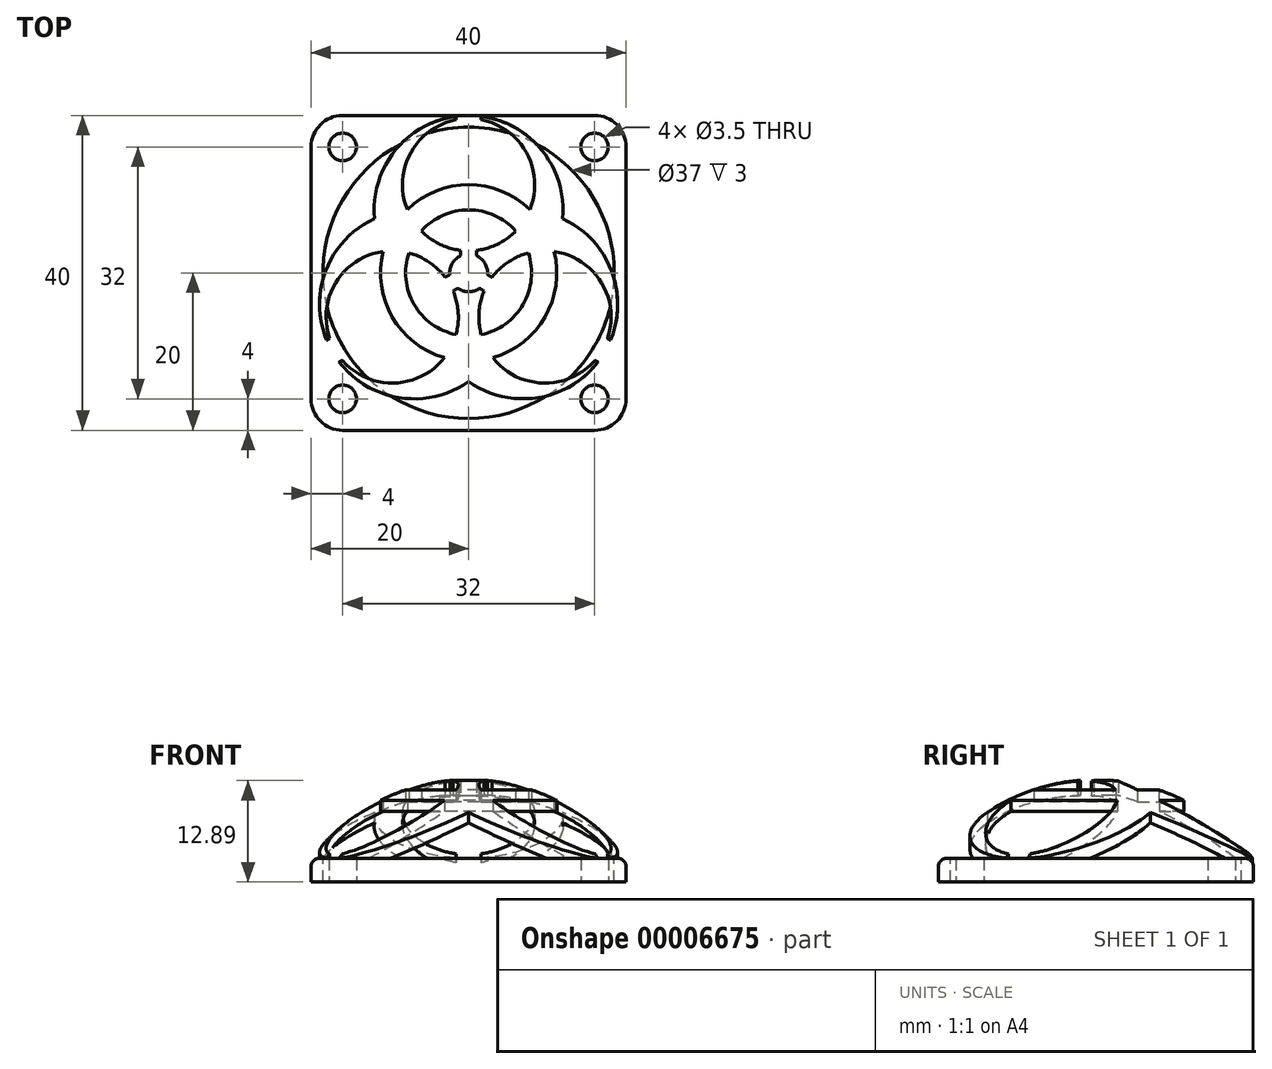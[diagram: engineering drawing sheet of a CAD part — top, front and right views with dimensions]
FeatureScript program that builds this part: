
annotation { "Feature Type Name" : "Feature", "Feature Type Description" : "" }
export const myFeature = defineFeature(function(context is Context, id is Id, definition is map)
    precondition{}
    {
        {
            var Q0;
            Q0=qCreatedBy(makeId("Top.planeOp"),FACE);
            var sketch = newSketch(context, id + "F0", { "sketchPlane" : qUnion([Q0])});
            skLineSegment(sketch, "E0.bottom", {"start": v(0, 0) * mm, "end": v(40, 0) * mm});
            skLineSegment(sketch, "E0.top", {"start": v(0, 40) * mm, "end": v(40, 40) * mm});
            skLineSegment(sketch, "E0.left", {"start": v(0, 0) * mm, "end": v(0, 40) * mm});
            skLineSegment(sketch, "E0.right", {"start": v(40, 0) * mm, "end": v(40, 40) * mm});
            skSolve(sketch);
        }
        {
            var Q0;
            Q0 = qSketchRegion(id + "F0", true);
            extrude(context, id + "F1", {"entities" : qUnion([Q0]), "depth" : 3 * mm});
        }
        {
            var Q0;
            Q0=makeQuery(id+"F1.opExtrude","CAP_FACE",FACE,{"disambiguationData":[OSD([sQuery(id+"F0.wireOp",EDGE,"E0.bottom"),sQuery(id+"F0.wireOp",EDGE,"E0.top"),sQuery(id+"F0.wireOp",EDGE,"E0.left"),sQuery(id+"F0.wireOp",EDGE,"E0.right")])],"isStart":false});
            var sketch = newSketch(context, id + "F2", { "sketchPlane" : qUnion([Q0])});
            skCircle(sketch, "E1", {"center": v(20, 20) * mm, "radius": 18.5 * mm});
            skSolve(sketch);
        }
        {
            var Q0;
            Q0 = qSketchRegion(id + "F2", true);
            extrude(context, id + "F3", {"entities" : qUnion([Q0]), "operationType" : NewBodyOperationType.REMOVE, "endBound" : BoundingType.THROUGH_ALL, "oppositeDirection" : true, "depth" : 25 * mm});
        }
        {
            var Q0;
            Q0=makeQuery(id+"F1.opExtrude","SWEPT_EDGE",EDGE,{"disambiguationData":[OSD([sQuery(id+"F0.wireOp",EDGE,"E0.top"),sQuery(id+"F0.wireOp",EDGE,"E0.right")])]});
            var Q1;
            Q1=makeQuery(id+"F1.opExtrude","SWEPT_EDGE",EDGE,{"disambiguationData":[OSD([sQuery(id+"F0.wireOp",EDGE,"E0.bottom"),sQuery(id+"F0.wireOp",EDGE,"E0.right")])]});
            var Q2;
            Q2=makeQuery(id+"F1.opExtrude","SWEPT_EDGE",EDGE,{"disambiguationData":[OSD([sQuery(id+"F0.wireOp",EDGE,"E0.top"),sQuery(id+"F0.wireOp",EDGE,"E0.left")])]});
            var Q3;
            Q3=makeQuery(id+"F1.opExtrude","SWEPT_EDGE",EDGE,{"disambiguationData":[OSD([sQuery(id+"F0.wireOp",EDGE,"E0.bottom"),sQuery(id+"F0.wireOp",EDGE,"E0.left")])]});
            fillet(context, id + "F4", {"entities" : qUnion([Q0, Q1, Q2, Q3]), "radius" : 4 * mm, "tangentPropagation" : true, "allowEdgeOverflow" : false});
        }
        {
            var Q0;
            Q0=makeQuery(id+"F1.opExtrude","CAP_FACE",FACE,{"disambiguationData":[OSD([sQuery(id+"F0.wireOp",EDGE,"E0.bottom"),sQuery(id+"F0.wireOp",EDGE,"E0.top"),sQuery(id+"F0.wireOp",EDGE,"E0.left"),sQuery(id+"F0.wireOp",EDGE,"E0.right")])],"isStart":true});
            var sketch = newSketch(context, id + "F5", { "sketchPlane" : qUnion([Q0])});
            skArc(sketch, "E2", {"start": v(21, -22.18) * mm, "mid": v(22.08, -21.2) * mm, "end": v(22.39, -19.78) * mm});
            skArc(sketch, "E3", {"start": v(18.4, -12.16) * mm, "mid": v(13.07, -16) * mm, "end": v(12.41, -22.53) * mm});
            skArc(sketch, "E4", {"start": v(30.87, -22.72) * mm, "mid": v(29.7, -14.4) * mm, "end": v(23.08, -9.23) * mm});
            skArc(sketch, "E5", {"start": v(31.95, -26.9) * mm, "mid": v(38.1, -20.4) * mm, "end": v(38.03, -11.44) * mm});
            skArc(sketch, "E6", {"start": v(20, -6.2) * mm, "mid": v(11.3, -4.13) * mm, "end": v(3.57, -8.67) * mm});
            skArc(sketch, "E7", {"start": v(12.21, -28.05) * mm, "mid": v(12.62, -35.2) * mm, "end": v(18.4, -39.45) * mm});
            skArc(sketch, "E8", {"start": v(21.6, -12.16) * mm, "mid": v(21.32, -14.96) * mm, "end": v(21.98, -17.7) * mm});
            skArc(sketch, "E9", {"start": v(12.41, -22.53) * mm, "mid": v(14.98, -21.38) * mm, "end": v(17.02, -19.44) * mm});
            skArc(sketch, "E10.trimOffspring", {"start": v(16.92, -9.23) * mm, "mid": v(10.3, -14.4) * mm, "end": v(9.13, -22.72) * mm});
            skArc(sketch, "E11.trimOffspring", {"start": v(8.05, -26.9) * mm, "mid": v(10.61, -35.48) * mm, "end": v(18.4, -39.9) * mm});
            skArc(sketch, "E12.trimOffspring", {"start": v(12.21, -28.05) * mm, "mid": v(20, -31.2) * mm, "end": v(27.79, -28.05) * mm});
            skArc(sketch, "E13.trimOffspring", {"start": v(14.01, -25.3) * mm, "mid": v(20, -28) * mm, "end": v(25.99, -25.3) * mm});
            skArc(sketch, "E14.trimOffspring", {"start": v(27.59, -22.53) * mm, "mid": v(26.93, -16) * mm, "end": v(21.6, -12.16) * mm});
            skArc(sketch, "E15.trimOffspring", {"start": v(16.92, -9.23) * mm, "mid": v(10.52, -6) * mm, "end": v(3.96, -8.9) * mm});
            skArc(sketch, "E16.trimOffspring", {"start": v(30.87, -22.72) * mm, "mid": v(36.86, -18.79) * mm, "end": v(37.64, -11.66) * mm});
            skArc(sketch, "E17.trimOffspring", {"start": v(25.99, -25.3) * mm, "mid": v(23.7, -23.66) * mm, "end": v(21, -22.86) * mm});
            skLineSegment(sketch, "E18.trimOffspring", {"start": v(36.04, -8.9) * mm, "end": v(36.43, -8.67) * mm});
            skLineSegment(sketch, "E19.trimOffspring", {"start": v(37.64, -11.66) * mm, "end": v(38.03, -11.44) * mm});
            skLineSegment(sketch, "E20.trimOffspring", {"start": v(3.96, -8.9) * mm, "end": v(3.57, -8.67) * mm});
            skLineSegment(sketch, "E21.trimOffspring", {"start": v(2.36, -11.66) * mm, "end": v(1.97, -11.44) * mm});
            skLineSegment(sketch, "E22.trimOffspring", {"start": v(18.4, -39.45) * mm, "end": v(18.4, -39.9) * mm});
            skLineSegment(sketch, "E23.trimOffspring", {"start": v(21.6, -39.45) * mm, "end": v(21.6, -39.9) * mm});
            skArc(sketch, "E24.trimOffspring", {"start": v(21.6, -39.9) * mm, "mid": v(29.39, -35.48) * mm, "end": v(31.95, -26.9) * mm});
            skArc(sketch, "E25.trimOffspring", {"start": v(21.6, -39.45) * mm, "mid": v(27.38, -35.2) * mm, "end": v(27.79, -28.05) * mm});
            skArc(sketch, "E26.trimOffspring", {"start": v(1.97, -11.44) * mm, "mid": v(1.9, -20.4) * mm, "end": v(8.05, -26.9) * mm});
            skArc(sketch, "E27.trimOffspring", {"start": v(2.36, -11.66) * mm, "mid": v(3.14, -18.79) * mm, "end": v(9.13, -22.72) * mm});
            skArc(sketch, "E28.trimOffspring", {"start": v(36.43, -8.67) * mm, "mid": v(28.7, -4.13) * mm, "end": v(20, -6.2) * mm});
            skArc(sketch, "E29.trimOffspring", {"start": v(36.04, -8.9) * mm, "mid": v(29.48, -6) * mm, "end": v(23.08, -9.23) * mm});
            skLineSegment(sketch, "E30.0", {"start": v(22.39, -19.78) * mm, "end": v(22.98, -19.44) * mm});
            skLineSegment(sketch, "E31.0", {"start": v(21.39, -18.04) * mm, "end": v(21.98, -17.7) * mm});
            skLineSegment(sketch, "E32.trimOffspring", {"start": v(21, -22.18) * mm, "end": v(21, -22.86) * mm});
            skLineSegment(sketch, "E33.trimOffspring", {"start": v(19, -22.18) * mm, "end": v(19, -22.86) * mm});
            skArc(sketch, "E34.trimOffspring", {"start": v(19, -22.86) * mm, "mid": v(16.3, -23.66) * mm, "end": v(14.01, -25.3) * mm});
            skArc(sketch, "E35.trimOffspring", {"start": v(17.61, -19.78) * mm, "mid": v(17.92, -21.2) * mm, "end": v(19, -22.18) * mm});
            skArc(sketch, "E36.trimOffspring", {"start": v(18.02, -17.7) * mm, "mid": v(18.68, -14.96) * mm, "end": v(18.4, -12.16) * mm});
            skLineSegment(sketch, "E37.trimOffspring", {"start": v(17.61, -19.78) * mm, "end": v(17.02, -19.44) * mm});
            skLineSegment(sketch, "E38.trimOffspring", {"start": v(18.61, -18.04) * mm, "end": v(18.02, -17.7) * mm});
            skArc(sketch, "E39.trimOffspring", {"start": v(22.98, -19.44) * mm, "mid": v(25.02, -21.38) * mm, "end": v(27.59, -22.53) * mm});
            skArc(sketch, "E40.trimOffspring", {"start": v(21.39, -18.04) * mm, "mid": v(20, -17.6) * mm, "end": v(18.61, -18.04) * mm});
            skSolve(sketch);
        }
        {
            var Q0;
            Q0 = qSketchRegion(id + "F5", true);
            extrude(context, id + "F6", {"entities" : qUnion([Q0]), "operationType" : NewBodyOperationType.ADD, "oppositeDirection" : true, "depth" : 13 * mm});
        }
        {
            var Q0;
            Q0=makeQuery(id+"FjeCkzkLcHHee1b_1.boolean.opBoolean","MERGE",FACE,{"derivedFrom":[makeQuery(id+"F1.opExtrude","CAP_FACE",FACE,{"disambiguationData":[OSD([sQuery(id+"F0.wireOp",EDGE,"E0.bottom"),sQuery(id+"F0.wireOp",EDGE,"E0.top"),sQuery(id+"F0.wireOp",EDGE,"E0.left"),sQuery(id+"F0.wireOp",EDGE,"E0.right")])],"isStart":true}),makeQuery(id+"FjeCkzkLcHHee1b_1.opExtrude","CAP_FACE",FACE,{"disambiguationData":[OSD([sQuery(id+"F5.wireOp",EDGE,"7c20ee55-d37f-477f-afb5-8cb142e75371"),sQuery(id+"F5.wireOp",EDGE,"c322b40b-e669-45d5-af77-03e13278a6a1"),sQuery(id+"F5.wireOp",EDGE,"64b58e43-a7cc-44bb-8f8e-211b15f0d819"),sQuery(id+"F5.wireOp",EDGE,"abb0b6dd-b8af-4ed5-96f3-eb897623521e"),sQuery(id+"F5.wireOp",EDGE,"94c6cc29-0406-4ddc-a4af-f0174a4eb0ba"),sQuery(id+"F5.wireOp",EDGE,"89b530f0-1eb4-48e8-a954-7e2e63659885.trimOffspring"),sQuery(id+"F5.wireOp",EDGE,"6c0d8bbc-d83f-41d6-aab6-746861fa3e45.trimOffspring"),sQuery(id+"F5.wireOp",EDGE,"393881ea-8ec9-4d60-8f85-3c2612d365ee.0"),sQuery(id+"F5.wireOp",EDGE,"c3659549-6018-4f88-8042-bb78193a6968.0"),sQuery(id+"F5.wireOp",EDGE,"acaf3530-5692-4ab2-ac0c-7444e3d4fef5.0"),sQuery(id+"F5.wireOp",EDGE,"3c889357-e91b-4824-be31-69f81962fded.0"),sQuery(id+"F5.wireOp",EDGE,"f8aa98c5-1780-4126-bf54-124605e78c8d.0"),sQuery(id+"F5.wireOp",EDGE,"d1cc962a-de2c-4229-abc7-ad092e9f673f.0"),sQuery(id+"F5.wireOp",EDGE,"ce528f82-5ef6-4796-b240-44a6564326f1.trimOffspring"),sQuery(id+"F5.wireOp",EDGE,"aea01dd2-4388-4872-9534-35a8ebe6cbda.trimOffspring"),sQuery(id+"F5.wireOp",EDGE,"10620485-125e-4d00-8166-1c2b6e97d19d.trimOffspring"),sQuery(id+"F5.wireOp",EDGE,"3cae6339-57ca-4c16-95d8-d688adb5fe67.trimOffspring"),sQuery(id+"F5.wireOp",EDGE,"7b890cfa-4926-411f-ba6b-3eb5ff1dca14.trimOffspring"),sQuery(id+"F5.wireOp",EDGE,"3cebedd4-9ec4-4957-bfb4-c5b9375723c5.trimOffspring"),sQuery(id+"F5.wireOp",EDGE,"45c4118b-560e-49fc-b60c-700372c17f42.trimOffspring"),sQuery(id+"F5.wireOp",EDGE,"5d7c18b5-ad8d-4647-a74f-bccac9c33e3d.trimOffspring"),sQuery(id+"F5.wireOp",EDGE,"9087e35b-6f35-4a95-a134-c9931716c53a.trimOffspring"),sQuery(id+"F5.wireOp",EDGE,"e9376375-5c43-4ebc-a500-b79f36a27335.trimOffspring"),sQuery(id+"F5.wireOp",EDGE,"6eddd865-cab9-4635-9fc5-55ac99587787.trimOffspring"),sQuery(id+"F5.wireOp",EDGE,"dde5fa37-4262-4c12-aca0-dc206e42c697.trimOffspring"),sQuery(id+"F5.wireOp",EDGE,"b69a62a0-5ab3-401e-ac67-9032fdb0c65f.trimOffspring"),sQuery(id+"F5.wireOp",EDGE,"aa0ac785-9475-47dc-89ef-cf27f4a7193f.trimOffspring"),sQuery(id+"F5.wireOp",EDGE,"8138ca97-3a3d-4183-b84e-3e0df1b7a173"),sQuery(id+"F5.wireOp",EDGE,"9dc1244c-1b35-42a9-9325-c940e5997173.trimOffspring"),sQuery(id+"F5.wireOp",EDGE,"eaf34bc7-d989-4a55-b91e-dafaf966cdfd.trimOffspring"),sQuery(id+"F5.wireOp",EDGE,"a711e81f-716e-459c-b94b-c57a34a1bb44.trimOffspring"),sQuery(id+"F5.wireOp",EDGE,"c96c1473-21b6-43c5-841f-89e27c65cc55.trimOffspring"),sQuery(id+"F5.wireOp",EDGE,"d4efb399-7a33-4649-88a4-caaefa096cf5.trimOffspring"),sQuery(id+"F5.wireOp",EDGE,"44508c0a-4444-4839-9407-eb5611b13a45.trimOffspring"),sQuery(id+"F5.wireOp",EDGE,"8e44444c-61b0-48bb-8b8f-7004c99f61ff.trimOffspring"),sQuery(id+"F5.wireOp",EDGE,"4c6a0ad1-4738-465d-b6ab-33721f2a24fa.trimOffspring"),sQuery(id+"F5.wireOp",EDGE,"c670b948-7825-41a7-abf3-c99801d38d13.trimOffspring"),sQuery(id+"F5.wireOp",EDGE,"e19c1920-761f-41d2-a384-4e67f943313a.trimOffspring"),sQuery(id+"F5.wireOp",EDGE,"2b7a0f11-a6ac-42d7-ad8b-0f967f79d273.trimOffspring"),sQuery(id+"F5.wireOp",EDGE,"0a31a10e-5cba-42f2-8d3c-32e7c72f3866.trimOffspring"),sQuery(id+"F5.wireOp",EDGE,"96bfba53-92af-4f19-8a5f-0bef9ba87aef.trimOffspring")])],"isStart":true})]});
            var sketch = newSketch(context, id + "F7", { "sketchPlane" : qUnion([Q0])});
            skCircle(sketch, "E41", {"center": v(36, -36) * mm, "radius": 1.75 * mm});
            skCircle(sketch, "E42", {"center": v(4, -36) * mm, "radius": 1.75 * mm});
            skCircle(sketch, "E43", {"center": v(4, -4) * mm, "radius": 1.75 * mm});
            skCircle(sketch, "E44", {"center": v(36, -4) * mm, "radius": 1.75 * mm});
            skSolve(sketch);
        }
        {
            var Q0;
            Q0 = qSketchRegion(id + "F7", true);
            extrude(context, id + "F8", {"entities" : qUnion([Q0]), "operationType" : NewBodyOperationType.REMOVE, "endBound" : BoundingType.THROUGH_ALL, "oppositeDirection" : true, "depth" : 25 * mm});
        }
        {
            var Q0;
            Q0=qCreatedBy(makeId("Right.planeOp"),FACE);
            cPlane(context, id + "F9", {"entities" : qUnion([Q0]), "cplaneType" : CPlaneType.OFFSET, "offset" : 20 * mm, "width" : 150 * mm, "height" : 150 * mm});
        }
        {
            var Q0;
            Q0=qCreatedBy(id+"F9.planeOp",FACE);
            var sketch = newSketch(context, id + "F10", { "sketchPlane" : qUnion([Q0])});
            skLineSegment(sketch, "E45.0", {"start": v(20, 0) * mm, "end": v(20, 16.54) * mm, "construction": true});
            skFitSpline(sketch, "E46", {"points": [v(0, 3) * mm, v(20, 13) * mm, v(40, 3) * mm], "startDerivative": vector(33, 42) * mm, "endDerivative": vector(33, -42) * mm});
            skLineSegment(sketch, "E47", {"start": v(0, 3) * mm, "end": v(0, 15) * mm});
            skLineSegment(sketch, "E48.0", {"start": v(20, 15) * mm, "end": v(0, 15) * mm});
            skLineSegment(sketch, "E49", {"start": v(20, 13) * mm, "end": v(20, 15) * mm});
            skSolve(sketch);
        }
        {
            var Q0;
            Q0 = qSketchRegion(id + "F10", true);
            var Q1;
            Q1=sQuery(id+"F10.wireOp",EDGE,"E45.0");
            revolve(context, id + "F11", {"operationType" : NewBodyOperationType.REMOVE, "entities" : qUnion([Q0]), "axis" : qUnion([Q1]), "revolveType" : RevolveType.FULL, "oppositeDirection" : true});
        }
        {
            var Q0;
            Q0=qCreatedBy(id+"F9.planeOp",FACE);
            var sketch = newSketch(context, id + "F12", { "sketchPlane" : qUnion([Q0])});
            skLineSegment(sketch, "E50", {"start": v(1.5, 0) * mm, "end": v(20, 0) * mm});
            skLineSegment(sketch, "E51.0", {"start": v(1.5, 0) * mm, "end": v(1.5, 3) * mm});
            skLineSegment(sketch, "E52.0", {"start": v(20, 0) * mm, "end": v(20, 11) * mm});
            skFitSpline(sketch, "E53", {"points": [v(1.5, 3) * mm, v(20, 11) * mm, v(38.5, 3) * mm], "startDerivative": vector(30, 39) * mm, "endDerivative": vector(31.2, -32.29) * mm});
            skSolve(sketch);
        }
        {
            var Q0;
            Q0 = qSketchRegion(id + "F12", true);
            var Q1;
            Q1=sQuery(id+"F12.wireOp",EDGE,"E52.0");
            revolve(context, id + "F13", {"operationType" : NewBodyOperationType.REMOVE, "entities" : qUnion([Q0]), "axis" : qUnion([Q1]), "revolveType" : RevolveType.FULL, "oppositeDirection" : true});
        }
        {
            var Q0;
            Q0=makeQuery(id+"F1.opExtrude","CAP_EDGE",EDGE,{"disambiguationData":[OSD([sQuery(id+"F0.wireOp",EDGE,"E0.right")])],"isStart":false});
            fillet(context, id + "F14", {"entities" : qUnion([Q0]), "radius" : 1 * mm, "tangentPropagation" : true, "allowEdgeOverflow" : false});
        }
    });
